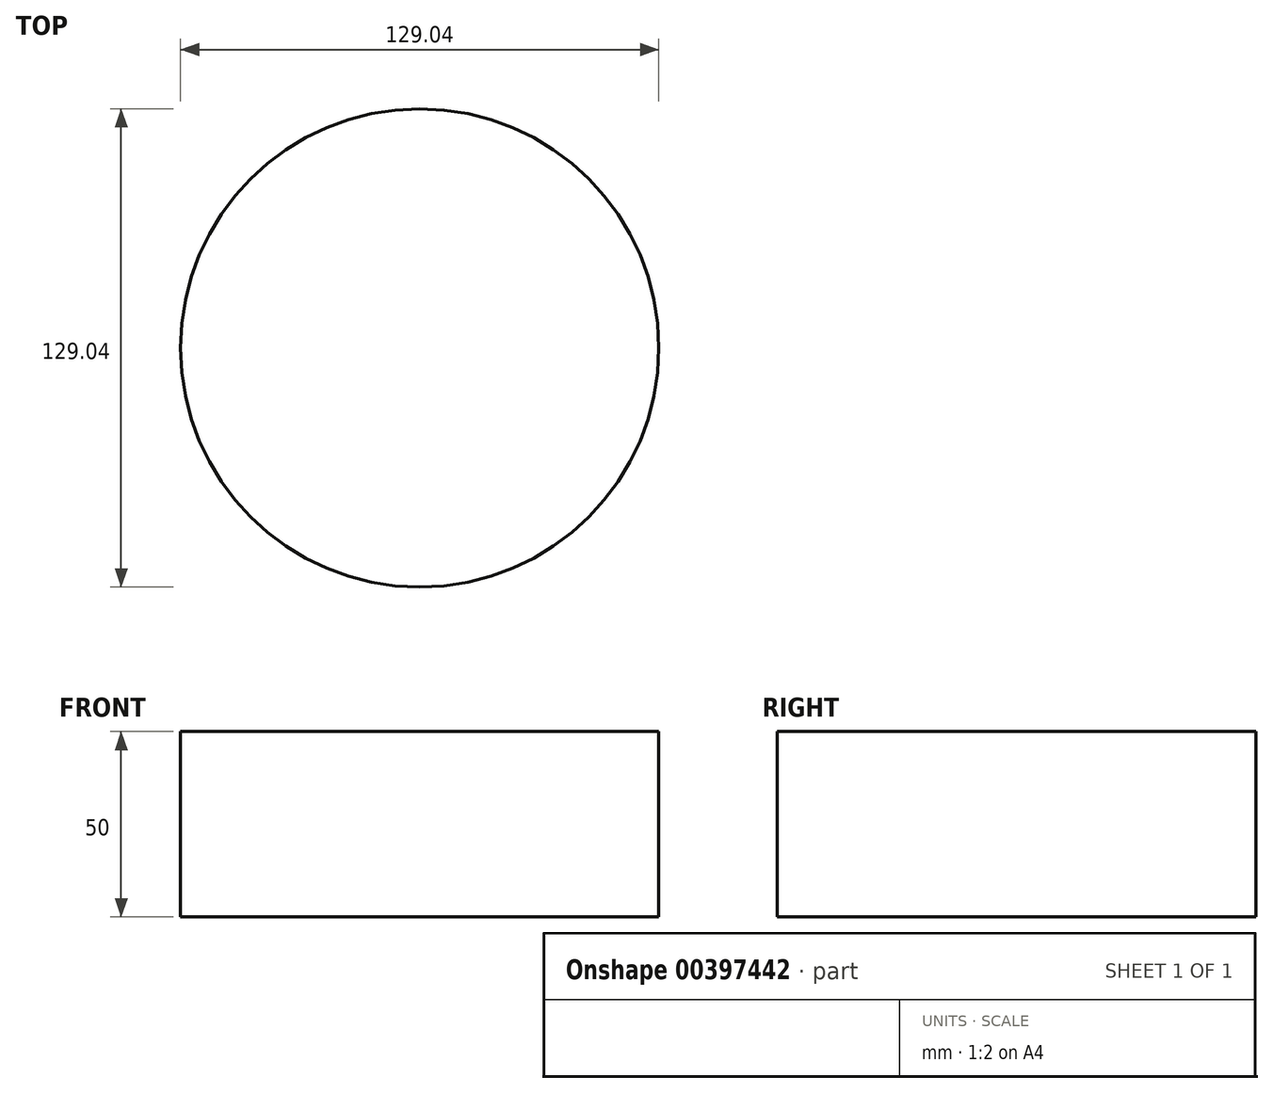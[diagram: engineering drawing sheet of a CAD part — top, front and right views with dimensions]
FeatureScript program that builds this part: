
annotation { "Feature Type Name" : "Feature", "Feature Type Description" : "" }
export const myFeature = defineFeature(function(context is Context, id is Id, definition is map)
    precondition{}
    {
        {
            var Q0;
            Q0=qCreatedBy(makeId("Top.planeOp"),FACE);
            var sketch = newSketch(context, id + "F0", { "sketchPlane" : qUnion([Q0])});
            skCircle(sketch, "E0", {"center": v(0, 0) * mm, "radius": 64.52 * mm});
            skSolve(sketch);
        }
        {
            var Q0;
            Q0 = qSketchRegion(id + "F0", true);
            extrude(context, id + "F1", {"entities" : qUnion([Q0]), "oppositeDirection" : true, "depth" : 25 * mm, "hasSecondDirection" : true, "secondDirectionOppositeDirection" : false, "secondDirectionDepth" : 25 * mm});
        }
    });
